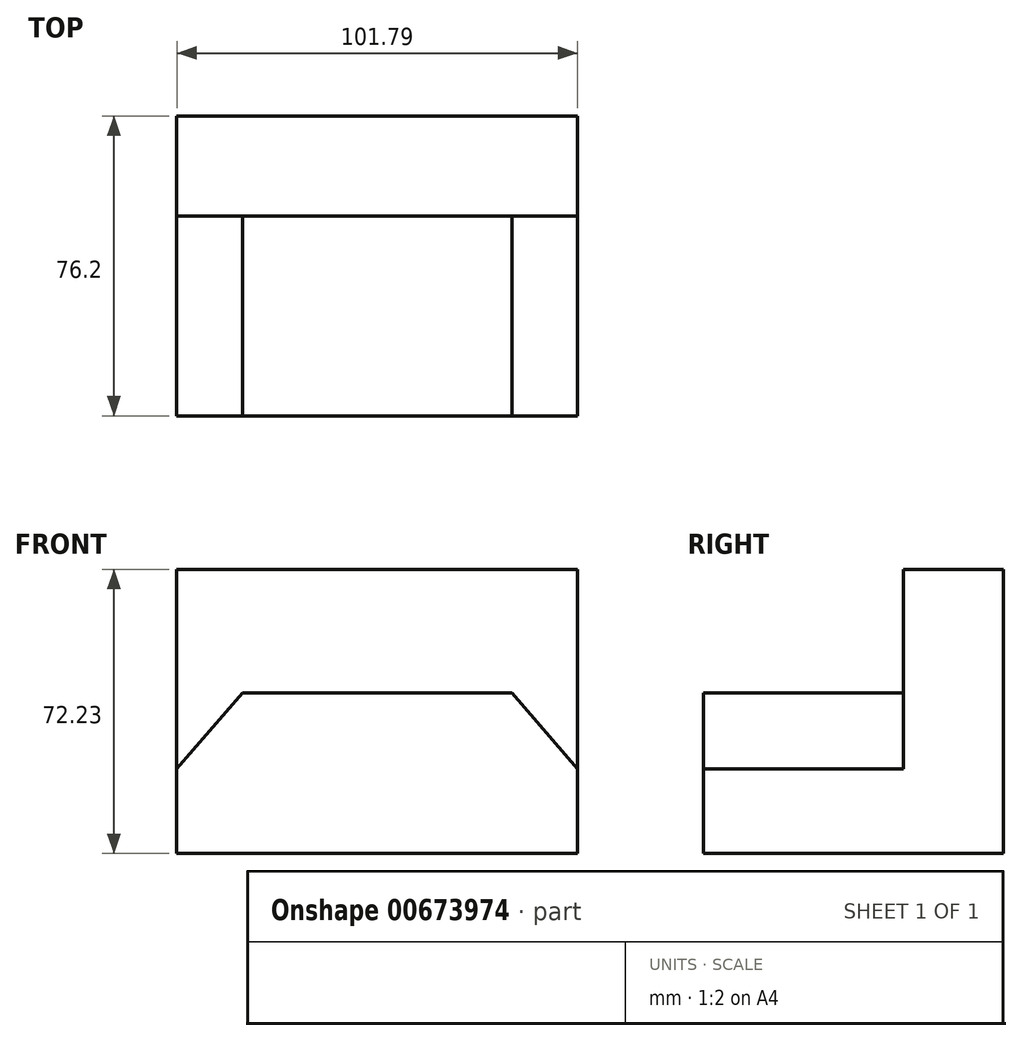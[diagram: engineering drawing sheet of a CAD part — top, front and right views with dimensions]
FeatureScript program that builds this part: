
annotation { "Feature Type Name" : "Feature", "Feature Type Description" : "" }
export const myFeature = defineFeature(function(context is Context, id is Id, definition is map)
    precondition{}
    {
        {
            var Q0;
            Q0=qCreatedBy(makeId("Front.planeOp"),FACE);
            var sketch = newSketch(context, id + "F0", { "sketchPlane" : qUnion([Q0])});
            skLineSegment(sketch, "E0.bottom", {"start": v(51.23, 31.45) * mm, "end": v(-50.56, 31.45) * mm});
            skLineSegment(sketch, "E0.top", {"start": v(51.23, -40.78) * mm, "end": v(-50.56, -40.78) * mm});
            skLineSegment(sketch, "E0.left", {"start": v(51.23, 31.45) * mm, "end": v(51.23, -40.78) * mm});
            skLineSegment(sketch, "E0.right", {"start": v(-50.56, 31.45) * mm, "end": v(-50.56, -40.78) * mm});
            skSolve(sketch);
        }
        {
            var Q0;
            Q0=makeQuery(id+"F0.imprint","IMPRINT",FACE,{"disambiguationData":[TD([[makeQuery(id+"F0.imprint","IMPRINT",EDGE,{"derivedFrom":sQuery(id+"F0.wireOp",EDGE,"E0.bottom")}),1.0]])]});
            extrude(context, id + "F1", {"entities" : qUnion([Q0]), "oppositeDirection" : true, "depth" : 25.4 * mm, "offsetDistance" : 25.4 * mm});
        }
        {
            var Q0;
            Q0=makeQuery(id+"F1.opExtrude","CAP_FACE",FACE,{"disambiguationData":[OSD([sQuery(id+"F0.wireOp",EDGE,"E0.bottom"),sQuery(id+"F0.wireOp",EDGE,"E0.top"),sQuery(id+"F0.wireOp",EDGE,"E0.left"),sQuery(id+"F0.wireOp",EDGE,"E0.right")])],"isStart":true});
            var sketch = newSketch(context, id + "F2", { "sketchPlane" : qUnion([Q0])});
            skLineSegment(sketch, "E1", {"start": v(-50.56, -19.22) * mm, "end": v(-33.9, 0) * mm});
            skLineSegment(sketch, "E2", {"start": v(51.23, -19.22) * mm, "end": v(34.56, 0) * mm});
            skLineSegment(sketch, "E3", {"start": v(34.56, 0) * mm, "end": v(-33.9, 0) * mm});
            skSolve(sketch);
        }
        {
            var Q0;
            {var subQ2=sQuery(id+"F2.wireOp",EDGE,"E1");Q0=makeQuery(id+"F2.imprint","IMPRINT",FACE,{"disambiguationData":[TD([[makeQuery(id+"F2.imprint","IMPRINT",EDGE,{"derivedFrom":subQ2}),-1.0]])]});}
            extrude(context, id + "F3", {"entities" : qUnion([Q0]), "operationType" : NewBodyOperationType.ADD, "depth" : 50.8 * mm, "offsetDistance" : 25.4 * mm});
        }
    });
